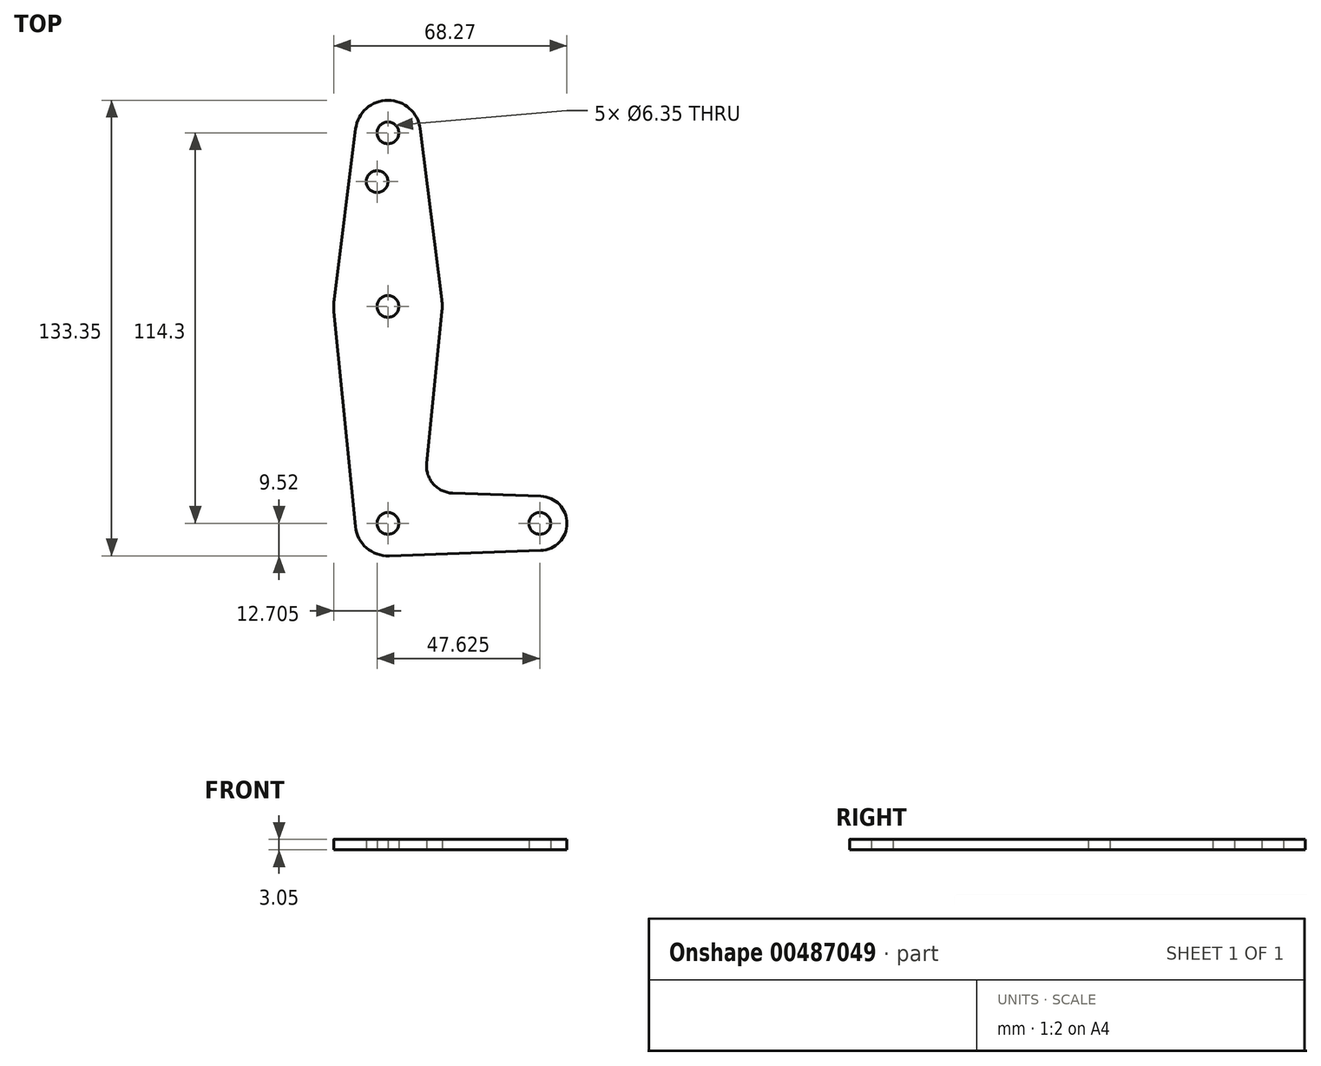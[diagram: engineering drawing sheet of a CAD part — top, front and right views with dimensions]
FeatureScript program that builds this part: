
annotation { "Feature Type Name" : "Feature", "Feature Type Description" : "" }
export const myFeature = defineFeature(function(context is Context, id is Id, definition is map)
    precondition{}
    {
        {
            var Q0;
            Q0=qCreatedBy(makeId("Top.planeOp"),FACE);
            var sketch = newSketch(context, id + "F0", { "sketchPlane" : qUnion([Q0])});
            skLineSegment(sketch, "E0", {"start": v(0, 0) * mm, "end": v(0, 114.3) * mm, "construction": true});
            skLineSegment(sketch, "E1", {"start": v(0, 0) * mm, "end": v(44.45, 0) * mm, "construction": true});
            skCircle(sketch, "E2", {"center": v(0, 0) * mm, "radius": 9.53 * mm});
            skCircle(sketch, "E3", {"center": v(0, 114.3) * mm, "radius": 9.53 * mm});
            skCircle(sketch, "E4", {"center": v(44.45, 0) * mm, "radius": 7.94 * mm});
            skCircle(sketch, "E5", {"center": v(0, 63.5) * mm, "radius": 15.88 * mm});
            skLineSegment(sketch, "E6", {"start": v(9.45, 115.5) * mm, "end": v(15.75, 65.48) * mm});
            skLineSegment(sketch, "E7", {"start": v(-9.45, 115.5) * mm, "end": v(-15.75, 65.48) * mm});
            skPoint(sketch, "E8.startSnap0", {"position": v(0, 57.15) * mm});
            skLineSegment(sketch, "E9", {"start": v(11.3, 17.6) * mm, "end": v(15.8, 61.9) * mm});
            skLineSegment(sketch, "E10", {"start": v(18.93, 8.85) * mm, "end": v(44.73, 7.93) * mm});
            skLineSegment(sketch, "E11", {"start": v(0.34, -9.52) * mm, "end": v(44.73, -7.93) * mm});
            skLineSegment(sketch, "E12", {"start": v(-15.8, 61.91) * mm, "end": v(-9.48, -0.95) * mm});
            skCircle(sketch, "E13", {"center": v(0, 114.3) * mm, "radius": 3.18 * mm});
            skCircle(sketch, "E14", {"center": v(-3.18, 100.03) * mm, "radius": 3.18 * mm});
            skCircle(sketch, "E15", {"center": v(0, 63.5) * mm, "radius": 3.18 * mm});
            skCircle(sketch, "E16", {"center": v(0, 0) * mm, "radius": 3.18 * mm});
            skCircle(sketch, "E17", {"center": v(44.45, 0) * mm, "radius": 3.17 * mm});
            skArc(sketch, "E18.filletArc", {"start": v(11.3, 17.6) * mm, "mid": v(13.22, 11.57) * mm, "end": v(18.93, 8.85) * mm});
            skSolve(sketch);
        }
        {
            var Q0;
            Q0=makeQuery(id+"F0.imprint","IMPRINT",FACE,{"disambiguationData":[TD([[makeQuery(id+"F0.imprint","IMPRINT",EDGE,{"derivedFrom":sQuery(id+"F0.wireOp",EDGE,"E13")}),-1.0]])]});
            var Q1;
            {var subQ0=sQuery(id+"F0.wireOp",EDGE,"E6");Q1=makeQuery(id+"F0.imprint","IMPRINT",FACE,{"disambiguationData":[TD([[makeQuery(id+"F0.imprint","IMPRINT",EDGE,{"derivedFrom":subQ0}),-1.0]])]});}
            var Q2;
            Q2=makeQuery(id+"F0.imprint","IMPRINT",FACE,{"disambiguationData":[TD([[makeQuery(id+"F0.imprint","IMPRINT",EDGE,{"derivedFrom":sQuery(id+"F0.wireOp",EDGE,"E15")}),-1.0]])]});
            var Q3;
            {var subQ0=sQuery(id+"F0.wireOp",EDGE,"E9");Q3=makeQuery(id+"F0.imprint","IMPRINT",FACE,{"disambiguationData":[TD([[makeQuery(id+"F0.imprint","IMPRINT",EDGE,{"derivedFrom":subQ0}),1.0]])]});}
            var Q4;
            Q4=makeQuery(id+"F0.imprint","IMPRINT",FACE,{"disambiguationData":[TD([[makeQuery(id+"F0.imprint","IMPRINT",EDGE,{"derivedFrom":sQuery(id+"F0.wireOp",EDGE,"E16")}),-1.0]])]});
            var Q5;
            Q5=makeQuery(id+"F0.imprint","IMPRINT",FACE,{"disambiguationData":[TD([[makeQuery(id+"F0.imprint","IMPRINT",EDGE,{"derivedFrom":sQuery(id+"F0.wireOp",EDGE,"E17")}),-1.0]])]});
            extrude(context, id + "F1", {"entities" : qUnion([Q0, Q1, Q2, Q3, Q4, Q5]), "depth" : 3.05 * mm});
        }
    });
